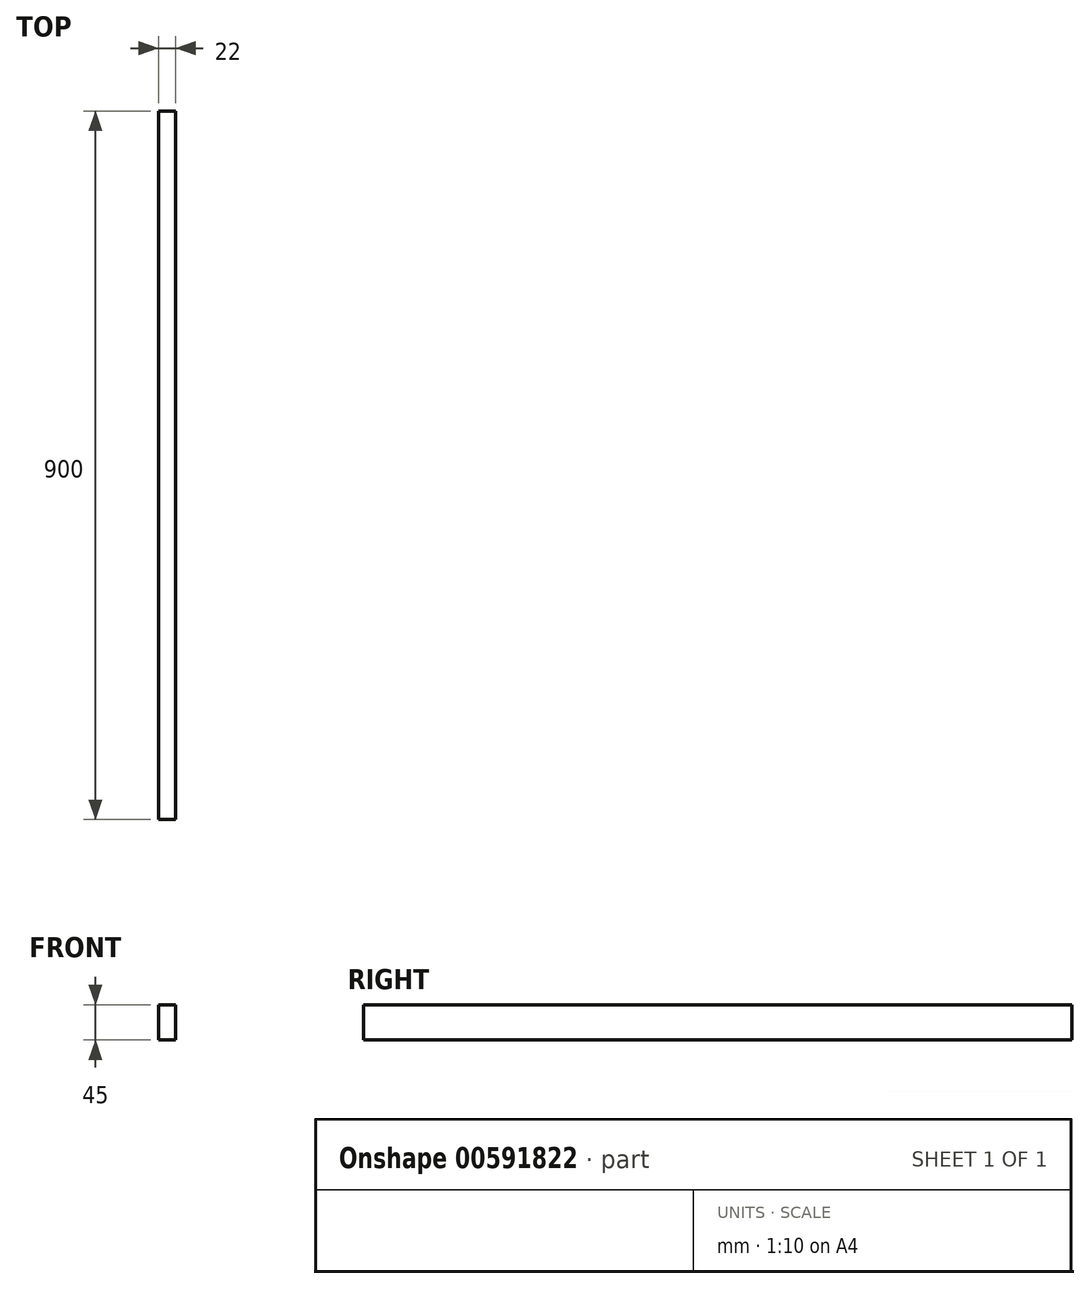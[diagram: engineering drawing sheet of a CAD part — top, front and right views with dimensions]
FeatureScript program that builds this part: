
annotation { "Feature Type Name" : "Feature", "Feature Type Description" : "" }
export const myFeature = defineFeature(function(context is Context, id is Id, definition is map)
    precondition{}
    {
        {
            var Q0;
            Q0=qCreatedBy(makeId("Front.planeOp"),FACE);
            var sketch = newSketch(context, id + "F0", { "sketchPlane" : qUnion([Q0])});
            skLineSegment(sketch, "E0.bottom", {"start": v(0, 0) * mm, "end": v(22, 0) * mm});
            skLineSegment(sketch, "E0.top", {"start": v(0, 45) * mm, "end": v(22, 45) * mm});
            skLineSegment(sketch, "E0.left", {"start": v(0, 0) * mm, "end": v(0, 45) * mm});
            skLineSegment(sketch, "E0.right", {"start": v(22, 0) * mm, "end": v(22, 45) * mm});
            skSolve(sketch);
        }
        {
            var Q0;
            Q0=qSketchRegion(id+"F0",true);
            extrude(context, id + "F1", {"entities" : qUnion([Q0]), "depth" : 900 * mm, "offsetDistance" : 25 * mm});
        }
    });
